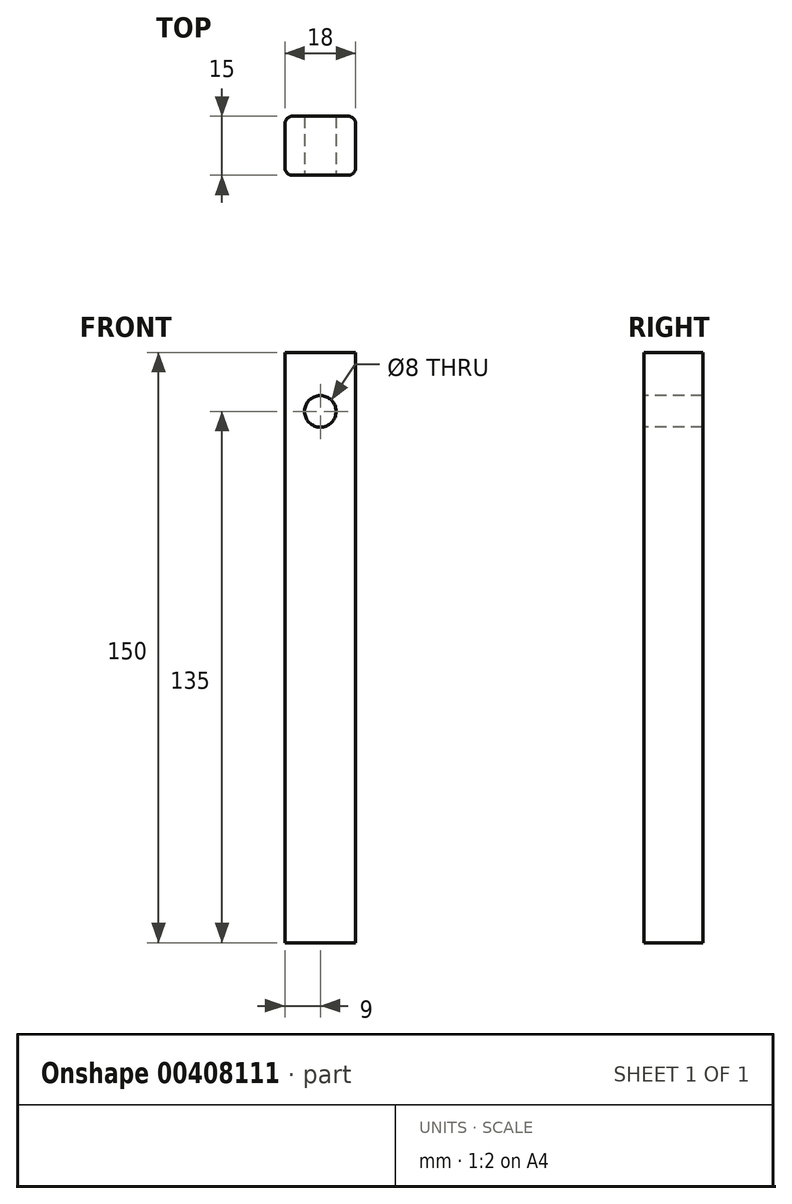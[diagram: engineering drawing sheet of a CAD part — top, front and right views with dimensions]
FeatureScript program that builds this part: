
annotation { "Feature Type Name" : "Feature", "Feature Type Description" : "" }
export const myFeature = defineFeature(function(context is Context, id is Id, definition is map)
    precondition{}
    {
        {
            var Q0;
            Q0=qCreatedBy(makeId("Front.planeOp"),FACE);
            var sketch = newSketch(context, id + "F0", { "sketchPlane" : qUnion([Q0])});
            skLineSegment(sketch, "E0.bottom", {"start": v(9, 75) * mm, "end": v(-9, 75) * mm});
            skLineSegment(sketch, "E0.top", {"start": v(9, -75) * mm, "end": v(-9, -75) * mm});
            skLineSegment(sketch, "E0.left", {"start": v(9, 75) * mm, "end": v(9, -75) * mm});
            skLineSegment(sketch, "E0.right", {"start": v(-9, 75) * mm, "end": v(-9, -75) * mm});
            skPoint(sketch, "E0.middle", {"position": v(0, 0) * mm});
            skSolve(sketch);
        }
        {
            var Q0;
            Q0=qSketchRegion(id+"F0",true);
            extrude(context, id + "F1", {"entities" : qUnion([Q0]), "endBound" : BoundingType.SYMMETRIC, "depth" : 15 * mm});
        }
        {
            var Q0;
            Q0=makeQuery(id+"F1.opExtrude","CAP_EDGE",EDGE,{"disambiguationData":[OSD([sQuery(id+"F0.wireOp",EDGE,"E0.right")])],"isStart":false});
            var Q1;
            Q1=makeQuery(id+"F1.opExtrude","CAP_EDGE",EDGE,{"disambiguationData":[OSD([sQuery(id+"F0.wireOp",EDGE,"E0.left")])],"isStart":false});
            var Q2;
            Q2=makeQuery(id+"F1.opExtrude","CAP_EDGE",EDGE,{"disambiguationData":[OSD([sQuery(id+"F0.wireOp",EDGE,"E0.left")])],"isStart":true});
            var Q3;
            Q3=makeQuery(id+"F1.opExtrude","CAP_EDGE",EDGE,{"disambiguationData":[OSD([sQuery(id+"F0.wireOp",EDGE,"E0.right")])],"isStart":true});
            fillet(context, id + "F2", {"entities" : qUnion([Q0, Q1, Q2, Q3]), "radius" : 2 * mm, "tangentPropagation" : true, "allowEdgeOverflow" : false});
        }
        {
            var Q0;
            Q0=makeQuery(id+"F1.opExtrude","CAP_FACE",FACE,{"disambiguationData":[OSD([sQuery(id+"F0.wireOp",EDGE,"E0.bottom"),sQuery(id+"F0.wireOp",EDGE,"E0.top"),sQuery(id+"F0.wireOp",EDGE,"E0.left"),sQuery(id+"F0.wireOp",EDGE,"E0.right")])],"isStart":false});
            var sketch = newSketch(context, id + "F3", { "sketchPlane" : qUnion([Q0])});
            skCircle(sketch, "E1", {"center": v(0, 60) * mm, "radius": 4 * mm});
            skSolve(sketch);
        }
        {
            var Q0;
            Q0 = qSketchRegion(id + "F3", true);
            extrude(context, id + "F4", {"entities" : qUnion([Q0]), "operationType" : NewBodyOperationType.REMOVE, "oppositeDirection" : true, "depth" : 25.4 * mm});
        }
    });
